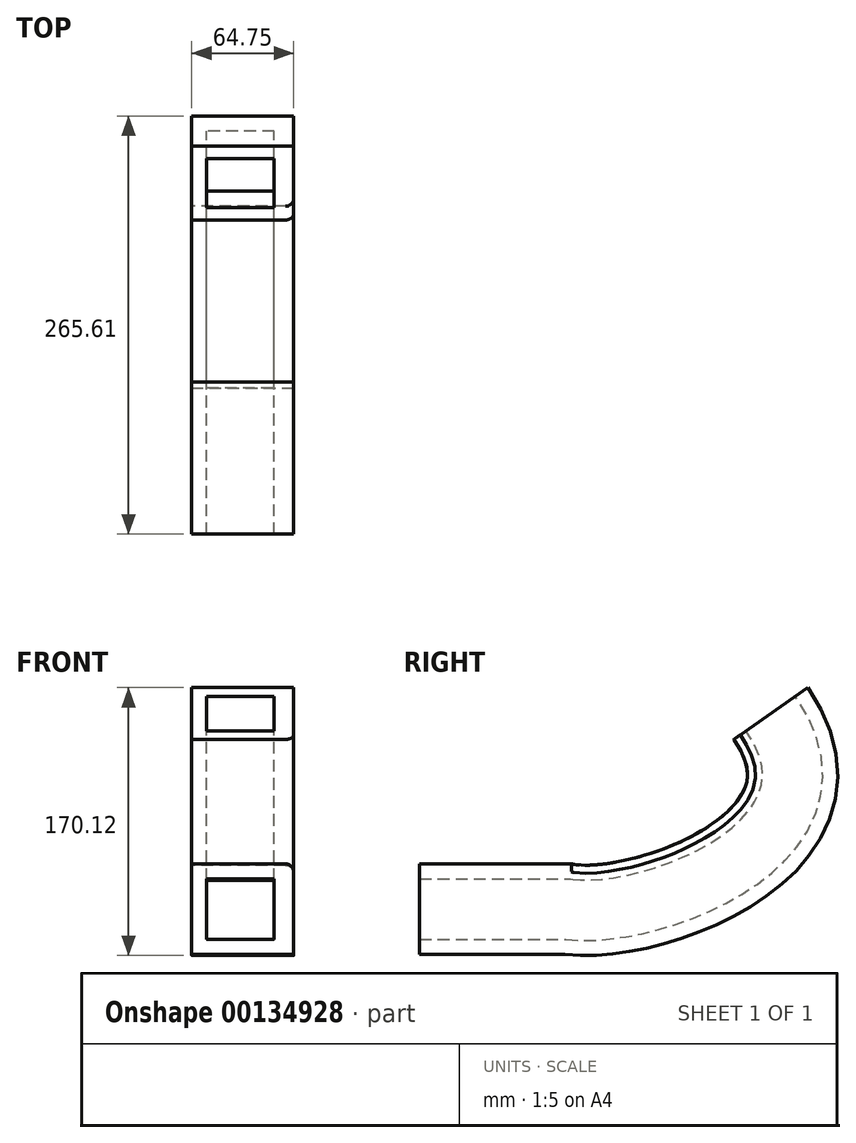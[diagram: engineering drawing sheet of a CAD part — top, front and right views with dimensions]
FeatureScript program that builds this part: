
annotation { "Feature Type Name" : "Feature", "Feature Type Description" : "" }
export const myFeature = defineFeature(function(context is Context, id is Id, definition is map)
    precondition{}
    {
        {
            var Q0;
            Q0=qCreatedBy(makeId("Front.planeOp"),FACE);
            var sketch = newSketch(context, id + "F0", { "sketchPlane" : qUnion([Q0])});
            skLineSegment(sketch, "E0.bottom", {"start": v(-32.68, 27.6) * mm, "end": v(32.07, 27.6) * mm});
            skLineSegment(sketch, "E0.top", {"start": v(-32.68, -29.75) * mm, "end": v(32.07, -29.75) * mm});
            skLineSegment(sketch, "E0.left", {"start": v(-32.68, 27.6) * mm, "end": v(-32.68, -29.75) * mm});
            skLineSegment(sketch, "E0.right", {"start": v(32.07, 27.6) * mm, "end": v(32.07, -29.75) * mm});
            skLineSegment(sketch, "E1.bottom", {"start": v(-23.12, 18.04) * mm, "end": v(19.73, 18.04) * mm});
            skLineSegment(sketch, "E1.top", {"start": v(-23.12, -20.2) * mm, "end": v(19.73, -20.2) * mm});
            skLineSegment(sketch, "E1.left", {"start": v(-23.12, 18.04) * mm, "end": v(-23.12, -20.2) * mm});
            skLineSegment(sketch, "E1.right", {"start": v(19.73, 18.04) * mm, "end": v(19.73, -20.2) * mm});
            skSolve(sketch);
        }
        {
            var Q0;
            Q0 = qSketchRegion(id + "F0", true);
            extrude(context, id + "F1", {"entities" : qUnion([Q0]), "depth" : 25.4 * mm});
        }
        {
            var Q0;
            Q0=qCreatedBy(makeId("Right.planeOp"),FACE);
            var sketch = newSketch(context, id + "F2", { "sketchPlane" : qUnion([Q0])});
            skLineSegment(sketch, "E2", {"start": v(0, 0) * mm, "end": v(69.11, 0) * mm});
            skFitSpline(sketch, "E3", {"points": [v(69.11, 0) * mm, v(196.75, 122.53) * mm], "startDerivative": vector(144.18, -22.93) * mm, "endDerivative": vector(-171.23, 244.88) * mm});
            skSolve(sketch);
        }
        {
            var Q0;
            Q0 = qSketchRegion(id + "F0", true);
            var Q1;
            Q1=sQuery(id+"F2.wireOp",EDGE,"E2");
            var Q2;
            Q2=sQuery(id+"F2.wireOp",EDGE,"E3");
            sweep(context, id + "F3", {"operationType" : NewBodyOperationType.ADD, "profiles" : qUnion([Q0]), "path" : qUnion([Q1, Q2])});
        }
        {
            var Q0;
            {var subQ0=sQuery(id+"F0.wireOp",EDGE,"E0.right");var subQ1=sQuery(id+"F0.wireOp",EDGE,"E0.bottom");Q0=makeQuery(id+"F3.boolean.opBoolean","MERGE",EDGE,{"derivedFrom":[makeQuery(id+"F1.opExtrude","SWEPT_EDGE",EDGE,{"disambiguationData":[OSD([subQ1,subQ0])]}),makeQuery(id+"F3.opSweep","SWEPT_EDGE",EDGE,{"disambiguationData":[OSD([subQ1,subQ0,sQuery(id+"F2.wireOp",EDGE,"E2")])]})]});}
            var Q1;
            Q1=makeQuery(id+"F3.opSweep","SWEPT_EDGE",EDGE,{"disambiguationData":[OSD([sQuery(id+"F0.wireOp",EDGE,"E0.bottom"),sQuery(id+"F0.wireOp",EDGE,"E0.right"),sQuery(id+"F2.wireOp",EDGE,"E3")]),OD(1.0)]});
            var Q2;
            Q2=makeQuery(id+"F3.opSweep","SWEPT_EDGE",EDGE,{"disambiguationData":[OSD([sQuery(id+"F0.wireOp",EDGE,"E0.bottom"),sQuery(id+"F0.wireOp",EDGE,"E0.right"),sQuery(id+"F2.wireOp",EDGE,"E3")]),OD(0.0)]});
            fillet(context, id + "F4", {"entities" : qUnion([Q0, Q1, Q2]), "radius" : 5.08 * mm, "tangentPropagation" : true, "allowEdgeOverflow" : false});
        }
    });
